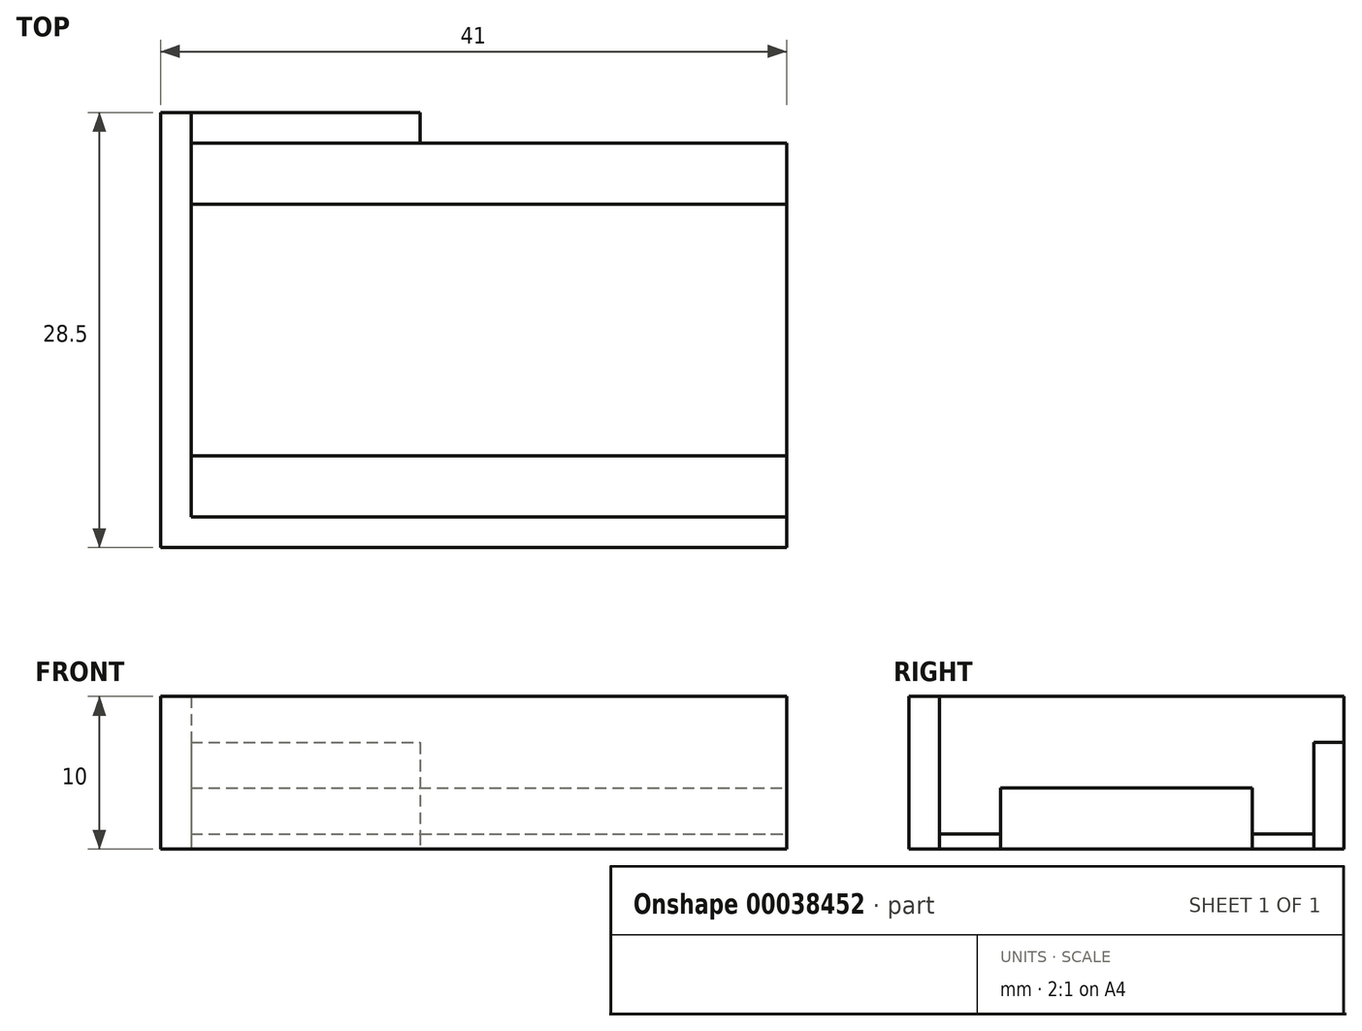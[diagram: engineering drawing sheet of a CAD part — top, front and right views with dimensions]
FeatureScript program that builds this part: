
annotation { "Feature Type Name" : "Feature", "Feature Type Description" : "" }
export const myFeature = defineFeature(function(context is Context, id is Id, definition is map)
    precondition{}
    {
        {
            var Q0;
            Q0=qCreatedBy(makeId("Top.planeOp"),FACE);
            var sketch = newSketch(context, id + "F0", { "sketchPlane" : qUnion([Q0])});
            skLineSegment(sketch, "E0.bottom", {"start": v(2, 26.5) * mm, "end": v(41, 26.5) * mm});
            skLineSegment(sketch, "E0.top", {"start": v(2, 2) * mm, "end": v(41, 2) * mm});
            skLineSegment(sketch, "E0.left", {"start": v(2, 26.5) * mm, "end": v(2, 2) * mm});
            skLineSegment(sketch, "E1.bottom", {"start": v(2, 22.5) * mm, "end": v(41, 22.5) * mm});
            skLineSegment(sketch, "E1.top", {"start": v(2, 6) * mm, "end": v(41, 6) * mm});
            skLineSegment(sketch, "E1.left", {"start": v(2, 22.5) * mm, "end": v(2, 6) * mm});
            skLineSegment(sketch, "E2.bottom", {"start": v(17, 26.5) * mm, "end": v(41, 26.5) * mm});
            skLineSegment(sketch, "E2.top", {"start": v(17, 28.5) * mm, "end": v(41, 28.5) * mm});
            skLineSegment(sketch, "E2.left", {"start": v(17, 26.5) * mm, "end": v(17, 28.5) * mm});
            skLineSegment(sketch, "E3.bottom", {"start": v(17, 28.5) * mm, "end": v(2, 28.5) * mm});
            skLineSegment(sketch, "E3.top", {"start": v(17, 26.5) * mm, "end": v(2, 26.5) * mm});
            skLineSegment(sketch, "E3.left", {"start": v(17, 28.5) * mm, "end": v(17, 26.5) * mm});
            skLineSegment(sketch, "E3.right", {"start": v(2, 28.5) * mm, "end": v(2, 26.5) * mm});
            skLineSegment(sketch, "E4.bottom", {"start": v(2, 28.5) * mm, "end": v(0, 28.5) * mm});
            skLineSegment(sketch, "E4.top", {"start": v(2, 2) * mm, "end": v(0, 2) * mm});
            skLineSegment(sketch, "E4.left", {"start": v(2, 28.5) * mm, "end": v(2, 2) * mm});
            skLineSegment(sketch, "E4.right", {"start": v(0, 28.5) * mm, "end": v(0, 2) * mm});
            skLineSegment(sketch, "E5.bottom", {"start": v(0, 2) * mm, "end": v(41, 2) * mm});
            skLineSegment(sketch, "E5.top", {"start": v(0, 0) * mm, "end": v(41, 0) * mm});
            skLineSegment(sketch, "E5.left", {"start": v(0, 2) * mm, "end": v(0, 0) * mm});
            skLineSegment(sketch, "E6", {"start": v(41, 28.5) * mm, "end": v(41, 0) * mm});
            skSolve(sketch);
        }
        {
            var Q0;
            {var subQ2=sQuery(id+"F0.wireOp",EDGE,"jjrR6PWR-H79K-9gla-FoHv-DC9FsdFlilEM.bottom");Q0=makeQuery(id+"F0.imprint","IMPRINT",FACE,{"disambiguationData":[TD([[makeQuery(id+"F0.imprint","IMPRINT",EDGE,{"derivedFrom":subQ2}),-1.0]])]});}
            var Q1;
            {var subQ1=sQuery(id+"F0.wireOp",EDGE,"E1.bottom");Q1=makeQuery(id+"F0.imprint","IMPRINT",FACE,{"disambiguationData":[TD([[makeQuery(id+"F0.imprint","IMPRINT",EDGE,{"derivedFrom":subQ1}),1.0]])]});}
            var Q2;
            {var subQ0=sQuery(id+"F0.wireOp",EDGE,"E1.top");Q2=makeQuery(id+"F0.imprint","IMPRINT",FACE,{"disambiguationData":[TD([[makeQuery(id+"F0.imprint","IMPRINT",EDGE,{"derivedFrom":subQ0}),-1.0]])]});}
            var Q3;
            Q3=makeQuery(id+"F0.imprint","IMPRINT",FACE,{"disambiguationData":[TD([[makeQuery(id+"F0.imprint","IMPRINT",EDGE,{"derivedFrom":sQuery(id+"F0.wireOp",EDGE,"jjrR6PWR-H79K-9gla-FoHv-DC9FsdFlilEM.right")}),1.0]])]});
            extrude(context, id + "F1", {"entities" : qUnion([Q0, Q1, Q2, Q3]), "depth" : 1 * mm});
        }
        {
            var Q0;
            {var subQ0=sQuery(id+"F0.wireOp",EDGE,"E1.bottom");Q0=makeQuery(id+"F0.imprint","IMPRINT",FACE,{"disambiguationData":[TD([[makeQuery(id+"F0.imprint","IMPRINT",EDGE,{"derivedFrom":subQ0}),-1.0]])]});}
            extrude(context, id + "F2", {"entities" : qUnion([Q0]), "depth" : 4 * mm});
        }
        {
            var Q0;
            {var subQ0=sQuery(id+"F0.wireOp",EDGE,"E3.bottom");Q0=makeQuery(id+"F0.imprint","IMPRINT",FACE,{"disambiguationData":[TD([[makeQuery(id+"F0.imprint","IMPRINT",EDGE,{"derivedFrom":subQ0}),1.0]])]});}
            extrude(context, id + "F3", {"entities" : qUnion([Q0]), "operationType" : NewBodyOperationType.ADD, "depth" : 7 * mm});
        }
        {
            var Q0;
            {var subQ0=sQuery(id+"F0.wireOp",EDGE,"E2.bottom");Q0=makeQuery(id+"F0.imprint","IMPRINT",FACE,{"disambiguationData":[TD([[makeQuery(id+"F0.imprint","IMPRINT",EDGE,{"derivedFrom":subQ0}),1.0]])]});}
            var Q1;
            {var subQ4=sQuery(id+"F0.wireOp",EDGE,"E4.bottom");Q1=makeQuery(id+"F0.imprint","IMPRINT",FACE,{"disambiguationData":[TD([[makeQuery(id+"F0.imprint","IMPRINT",EDGE,{"derivedFrom":subQ4}),1.0]])]});}
            var Q2;
            {var subQ1=sQuery(id+"F0.wireOp",EDGE,"E5.top");Q2=makeQuery(id+"F0.imprint","IMPRINT",FACE,{"disambiguationData":[TD([[makeQuery(id+"F0.imprint","IMPRINT",EDGE,{"derivedFrom":subQ1}),1.0]])]});}
            extrude(context, id + "F4", {"entities" : qUnion([Q0, Q1, Q2]), "depth" : 10 * mm});
        }
    });
